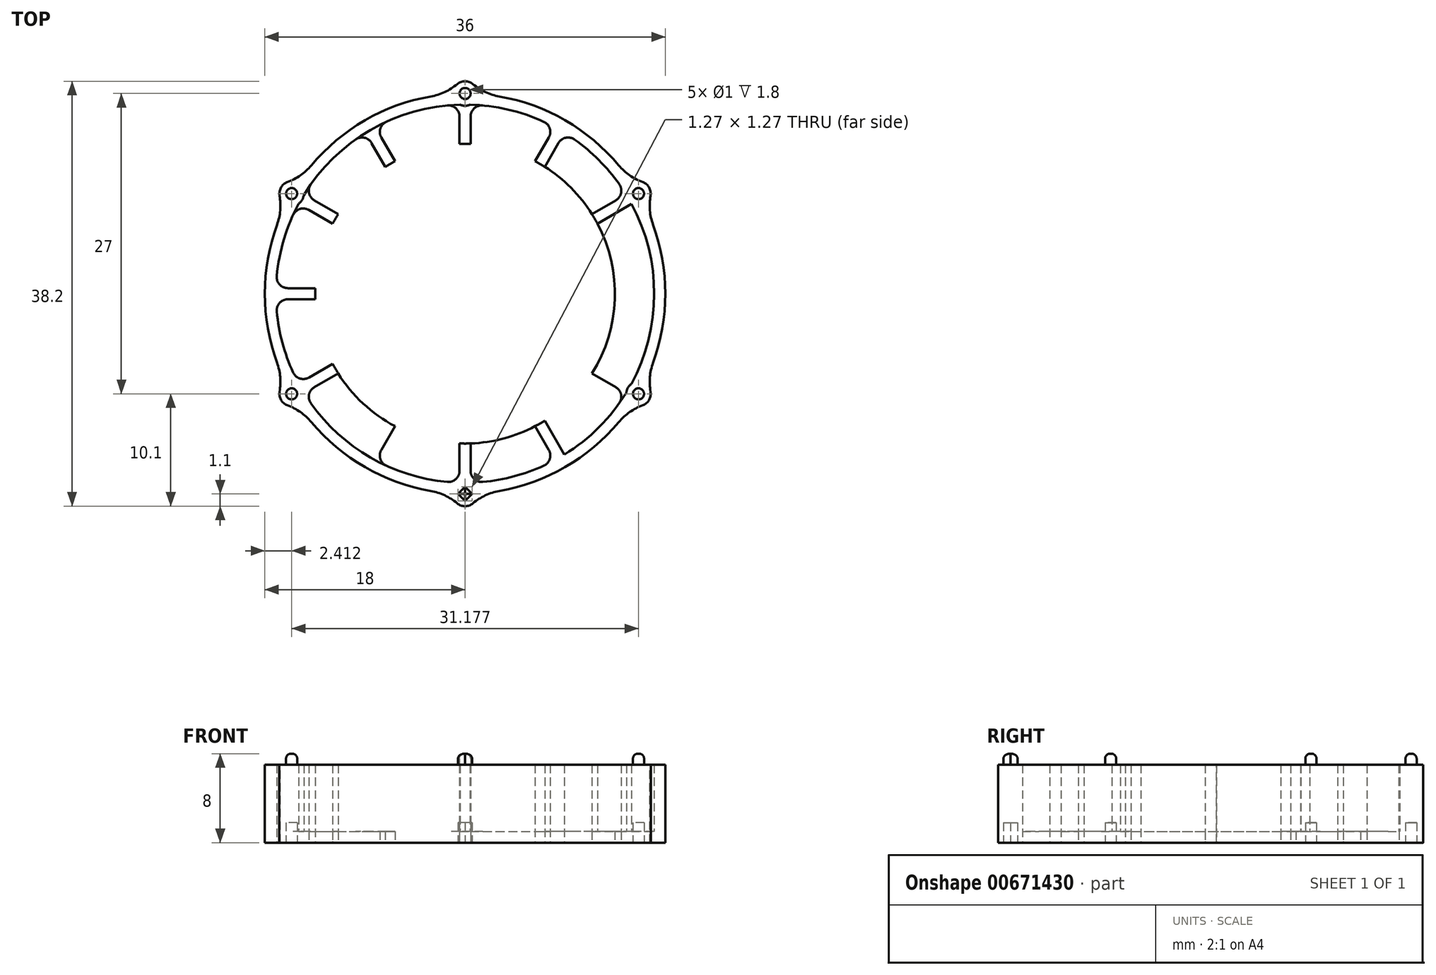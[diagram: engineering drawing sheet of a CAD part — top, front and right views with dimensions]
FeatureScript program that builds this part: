
annotation { "Feature Type Name" : "Feature", "Feature Type Description" : "" }
export const myFeature = defineFeature(function(context is Context, id is Id, definition is map)
    precondition{}
    {
        {
            var Q0;
            Q0=qCreatedBy(makeId("Top.planeOp"),FACE);
            var sketch = newSketch(context, id + "F0", { "sketchPlane" : qUnion([Q0])});
            skCircle(sketch, "E0", {"center": v(0, 0) * mm, "radius": 18 * mm});
            skCircle(sketch, "E1.0", {"center": v(0, 0) * mm, "radius": 17 * mm});
            skLineSegment(sketch, "E2.bottom", {"start": v(8.56, 15.83) * mm, "end": v(9.43, 15.33) * mm});
            skLineSegment(sketch, "E2.top", {"start": v(-9.43, -15.33) * mm, "end": v(-8.56, -15.83) * mm});
            skLineSegment(sketch, "E2.left", {"start": v(8.56, 15.83) * mm, "end": v(-9.43, -15.33) * mm});
            skLineSegment(sketch, "E2.right", {"start": v(9.43, 15.33) * mm, "end": v(-8.56, -15.83) * mm});
            skLineSegment(sketch, "E3.bottom", {"start": v(15.33, 9.43) * mm, "end": v(15.83, 8.56) * mm});
            skLineSegment(sketch, "E3.top", {"start": v(-15.83, -8.56) * mm, "end": v(-15.33, -9.43) * mm});
            skLineSegment(sketch, "E3.left", {"start": v(15.33, 9.43) * mm, "end": v(-15.83, -8.56) * mm});
            skLineSegment(sketch, "E3.right", {"start": v(15.83, 8.56) * mm, "end": v(-15.33, -9.43) * mm});
            skLineSegment(sketch, "E4", {"start": v(-38.35, 0) * mm, "end": v(39.17, 0) * mm, "construction": true});
            skLineSegment(sketch, "E5", {"start": v(0, 42.5) * mm, "end": v(0, -42.47) * mm, "construction": true});
            skLineSegment(sketch, "E6.bottom", {"start": v(-18, 0.5) * mm, "end": v(18, 0.5) * mm});
            skLineSegment(sketch, "E6.top", {"start": v(-18, -0.5) * mm, "end": v(18, -0.5) * mm});
            skLineSegment(sketch, "E6.left", {"start": v(-18, 0.5) * mm, "end": v(-18, -0.5) * mm});
            skLineSegment(sketch, "E6.right", {"start": v(18, 0.5) * mm, "end": v(18, -0.5) * mm});
            skLineSegment(sketch, "E7.bottom", {"start": v(-15.33, 9.43) * mm, "end": v(15.83, -8.56) * mm});
            skLineSegment(sketch, "E7.top", {"start": v(-15.83, 8.56) * mm, "end": v(15.33, -9.43) * mm});
            skLineSegment(sketch, "E7.left", {"start": v(-15.33, 9.43) * mm, "end": v(-15.83, 8.56) * mm});
            skLineSegment(sketch, "E7.right", {"start": v(15.83, -8.56) * mm, "end": v(15.33, -9.43) * mm});
            skLineSegment(sketch, "E8.bottom", {"start": v(-0.5, 18) * mm, "end": v(0.5, 18) * mm});
            skLineSegment(sketch, "E8.top", {"start": v(-0.5, -18) * mm, "end": v(0.5, -18) * mm});
            skLineSegment(sketch, "E8.left", {"start": v(-0.5, 18) * mm, "end": v(-0.5, -18) * mm});
            skLineSegment(sketch, "E8.right", {"start": v(0.5, 18) * mm, "end": v(0.5, -18) * mm});
            skLineSegment(sketch, "E9.bottom", {"start": v(-9.43, 15.33) * mm, "end": v(-8.56, 15.83) * mm});
            skLineSegment(sketch, "E9.top", {"start": v(8.56, -15.83) * mm, "end": v(9.43, -15.33) * mm});
            skLineSegment(sketch, "E9.left", {"start": v(-9.43, 15.33) * mm, "end": v(8.56, -15.83) * mm});
            skLineSegment(sketch, "E9.right", {"start": v(-8.56, 15.83) * mm, "end": v(9.43, -15.33) * mm});
            skCircle(sketch, "E10", {"center": v(0, 0) * mm, "radius": 13.47 * mm});
            skSolve(sketch);
        }
        {
            var Q0;
            Q0=qCreatedBy(makeId("Top.planeOp"),FACE);
            var sketch = newSketch(context, id + "F1", { "sketchPlane" : qUnion([Q0])});
            skCircle(sketch, "E11", {"center": v(0, 0) * mm, "radius": 18 * mm});
            skCircle(sketch, "E12", {"center": v(0, 0) * mm, "radius": 17 * mm});
            skSolve(sketch);
        }
        {
            var Q0;
            Q0=makeQuery(id+"F1.imprint","IMPRINT",FACE,{"disambiguationData":[TD([[makeQuery(id+"F1.imprint","IMPRINT",EDGE,{"derivedFrom":sQuery(id+"F1.wireOp",EDGE,"E11")}),1.0]])]});
            extrude(context, id + "F2", {"entities" : qUnion([Q0]), "depth" : 7 * mm, "offsetDistance" : 25 * mm});
        }
        {
            var Q0;
            {var subQ0=sQuery(id+"F0.wireOp",EDGE,"E2.right");var subQ1=sQuery(id+"F0.wireOp",EDGE,"E1.0");var subQ2=makeQuery(id+"F0.imprint","INTERSECT",VERTEX,{"disambiguationData":[OD(0.0)],"derivedFrom":[subQ1,subQ0]});Q0=makeQuery(id+"F0.imprint","IMPRINT",FACE,{"disambiguationData":[TD([[makeQuery(id+"F0.imprint","IMPRINT",EDGE,{"disambiguationData":[TD([[subQ2,-1.0]])],"derivedFrom":subQ1}),1.0]])]});}
            var Q1;
            {var subQ0=sQuery(id+"F0.wireOp",EDGE,"E8.left");var subQ1=sQuery(id+"F0.wireOp",EDGE,"E1.0");var subQ2=makeQuery(id+"F0.imprint","INTERSECT",VERTEX,{"disambiguationData":[OD(1.0)],"derivedFrom":[subQ1,subQ0]});Q1=makeQuery(id+"F0.imprint","IMPRINT",FACE,{"disambiguationData":[TD([[makeQuery(id+"F0.imprint","IMPRINT",EDGE,{"disambiguationData":[TD([[subQ2,-1.0]])],"derivedFrom":subQ1}),1.0]])]});}
            var Q2;
            {var subQ0=sQuery(id+"F0.wireOp",EDGE,"E3.left");var subQ1=sQuery(id+"F0.wireOp",EDGE,"E1.0");var subQ2=makeQuery(id+"F0.imprint","INTERSECT",VERTEX,{"disambiguationData":[OD(1.0)],"derivedFrom":[subQ1,subQ0]});Q2=makeQuery(id+"F0.imprint","IMPRINT",FACE,{"disambiguationData":[TD([[makeQuery(id+"F0.imprint","IMPRINT",EDGE,{"disambiguationData":[TD([[subQ2,-1.0]])],"derivedFrom":subQ1}),1.0]])]});}
            var Q3;
            {var subQ0=sQuery(id+"F0.wireOp",EDGE,"E3.right");var subQ1=sQuery(id+"F0.wireOp",EDGE,"E1.0");var subQ2=makeQuery(id+"F0.imprint","INTERSECT",VERTEX,{"disambiguationData":[OD(0.0)],"derivedFrom":[subQ1,subQ0]});Q3=makeQuery(id+"F0.imprint","IMPRINT",FACE,{"disambiguationData":[TD([[makeQuery(id+"F0.imprint","IMPRINT",EDGE,{"disambiguationData":[TD([[subQ2,-1.0]])],"derivedFrom":subQ1}),1.0]])]});}
            var Q4;
            {var subQ0=sQuery(id+"F0.wireOp",EDGE,"E9.left");var subQ1=sQuery(id+"F0.wireOp",EDGE,"E1.0");var subQ2=makeQuery(id+"F0.imprint","INTERSECT",VERTEX,{"disambiguationData":[OD(1.0)],"derivedFrom":[subQ1,subQ0]});Q4=makeQuery(id+"F0.imprint","IMPRINT",FACE,{"disambiguationData":[TD([[makeQuery(id+"F0.imprint","IMPRINT",EDGE,{"disambiguationData":[TD([[subQ2,-1.0]])],"derivedFrom":subQ1}),1.0]])]});}
            var Q5;
            {var subQ0=sQuery(id+"F0.wireOp",EDGE,"E6.bottom");var subQ1=sQuery(id+"F0.wireOp",EDGE,"E1.0");var subQ2=makeQuery(id+"F0.imprint","INTERSECT",VERTEX,{"disambiguationData":[OD(1.0)],"derivedFrom":[subQ1,subQ0]});Q5=makeQuery(id+"F0.imprint","IMPRINT",FACE,{"disambiguationData":[TD([[makeQuery(id+"F0.imprint","IMPRINT",EDGE,{"disambiguationData":[TD([[subQ2,-1.0]])],"derivedFrom":subQ1}),1.0]])]});}
            extrude(context, id + "F3", {"entities" : qUnion([Q0, Q1, Q2, Q3, Q4, Q5]), "operationType" : NewBodyOperationType.ADD, "depth" : 7 * mm, "offsetDistance" : 25 * mm});
        }
        {
            var Q0;
            Q0=makeQuery(id+"F1.imprint","IMPRINT",FACE,{"disambiguationData":[TD([[makeQuery(id+"F1.imprint","IMPRINT",EDGE,{"derivedFrom":sQuery(id+"F1.wireOp",EDGE,"E11")}),1.0]])]});
            var Q1;
            Q1=makeQuery(id+"F1.imprint","IMPRINT",FACE,{"disambiguationData":[TD([[makeQuery(id+"F1.imprint","IMPRINT",EDGE,{"derivedFrom":sQuery(id+"F1.wireOp",EDGE,"E12")}),1.0]])]});
            extrude(context, id + "F4", {"entities" : qUnion([Q0, Q1]), "operationType" : NewBodyOperationType.ADD, "depth" : 1 * mm, "offsetDistance" : 25 * mm});
        }
        {
            var Q0;
            Q0=qCreatedBy(makeId("Top.planeOp"),FACE);
            var sketch = newSketch(context, id + "F5", { "sketchPlane" : qUnion([Q0])});
            skCircle(sketch, "E13", {"center": v(0, 0) * mm, "radius": 18 * mm});
            skLineSegment(sketch, "E14", {"start": v(0, 18) * mm, "end": v(0, -18) * mm, "construction": true});
            skLineSegment(sketch, "E15", {"start": v(15.59, 9) * mm, "end": v(0, 0) * mm, "construction": true});
            skLineSegment(sketch, "E16", {"start": v(9, 15.59) * mm, "end": v(0, 0) * mm, "construction": true});
            skLineSegment(sketch, "E17", {"start": v(0, 0) * mm, "end": v(18, 0) * mm, "construction": true});
            skLineSegment(sketch, "E18", {"start": v(0, 0) * mm, "end": v(15.59, -9) * mm, "construction": true});
            skLineSegment(sketch, "E19", {"start": v(0, 0) * mm, "end": v(9, -15.59) * mm, "construction": true});
            skLineSegment(sketch, "E20", {"start": v(0, 0) * mm, "end": v(-9, 15.59) * mm, "construction": true});
            skLineSegment(sketch, "E21", {"start": v(0, 0) * mm, "end": v(-15.59, 9) * mm, "construction": true});
            skLineSegment(sketch, "E22", {"start": v(0, 0) * mm, "end": v(-18, 0) * mm, "construction": true});
            skLineSegment(sketch, "E23", {"start": v(0, 0) * mm, "end": v(-15.59, -9) * mm, "construction": true});
            skLineSegment(sketch, "E24", {"start": v(0, 0) * mm, "end": v(-9, -15.59) * mm, "construction": true});
            skCircle(sketch, "E25", {"center": v(0, 18) * mm, "radius": 1.1 * mm});
            skCircle(sketch, "E26", {"center": v(15.59, 9) * mm, "radius": 1.1 * mm});
            skCircle(sketch, "E27", {"center": v(15.59, -9) * mm, "radius": 1.1 * mm});
            skCircle(sketch, "E28", {"center": v(0, -18) * mm, "radius": 1.1 * mm});
            skCircle(sketch, "E29", {"center": v(-15.59, -9) * mm, "radius": 1.1 * mm});
            skCircle(sketch, "E30", {"center": v(-15.59, 9) * mm, "radius": 1.1 * mm});
            skCircle(sketch, "E31", {"center": v(-15.59, 9) * mm, "radius": 0.5 * mm});
            skCircle(sketch, "E32", {"center": v(0, 18) * mm, "radius": 0.5 * mm});
            skCircle(sketch, "E33", {"center": v(15.59, 9) * mm, "radius": 0.5 * mm});
            skCircle(sketch, "E34", {"center": v(15.59, -9) * mm, "radius": 0.5 * mm});
            skCircle(sketch, "E35", {"center": v(-15.59, -9) * mm, "radius": 0.5 * mm});
            skLineSegment(sketch, "E36.bottom", {"start": v(0.64, -18) * mm, "end": v(0, -18.64) * mm});
            skLineSegment(sketch, "E36.top", {"start": v(0, -17.36) * mm, "end": v(-0.64, -18) * mm});
            skLineSegment(sketch, "E36.left", {"start": v(0.64, -18) * mm, "end": v(0, -17.36) * mm});
            skLineSegment(sketch, "E36.right", {"start": v(0, -18.64) * mm, "end": v(-0.64, -18) * mm});
            skSolve(sketch);
        }
        {
            var Q0;
            {var subQ0=sQuery(id+"F5.wireOp",EDGE,"E30");var subQ1=sQuery(id+"F5.wireOp",EDGE,"E13");var subQ2=makeQuery(id+"F5.imprint","INTERSECT",VERTEX,{"disambiguationData":[OD(0.0)],"derivedFrom":[subQ1,subQ0]});Q0=makeQuery(id+"F5.imprint","IMPRINT",FACE,{"disambiguationData":[TD([[makeQuery(id+"F5.imprint","IMPRINT",EDGE,{"disambiguationData":[TD([[subQ2,-1.0]])],"derivedFrom":subQ1}),1.0]])]});}
            var Q1;
            {var subQ0=sQuery(id+"F5.wireOp",EDGE,"E30");var subQ1=sQuery(id+"F5.wireOp",EDGE,"E13");var subQ2=makeQuery(id+"F5.imprint","INTERSECT",VERTEX,{"disambiguationData":[OD(0.0)],"derivedFrom":[subQ1,subQ0]});Q1=makeQuery(id+"F5.imprint","IMPRINT",FACE,{"disambiguationData":[TD([[makeQuery(id+"F5.imprint","IMPRINT",EDGE,{"disambiguationData":[TD([[subQ2,-1.0]])],"derivedFrom":subQ1}),-1.0]])]});}
            var Q2;
            {var subQ0=sQuery(id+"F5.wireOp",EDGE,"E25");var subQ1=sQuery(id+"F5.wireOp",EDGE,"E13");var subQ2=makeQuery(id+"F5.imprint","INTERSECT",VERTEX,{"disambiguationData":[OD(0.0)],"derivedFrom":[subQ1,subQ0]});Q2=makeQuery(id+"F5.imprint","IMPRINT",FACE,{"disambiguationData":[TD([[makeQuery(id+"F5.imprint","IMPRINT",EDGE,{"disambiguationData":[TD([[subQ2,-1.0]])],"derivedFrom":subQ1}),1.0]])]});}
            var Q3;
            {var subQ0=sQuery(id+"F5.wireOp",EDGE,"E25");var subQ1=sQuery(id+"F5.wireOp",EDGE,"E13");var subQ2=makeQuery(id+"F5.imprint","INTERSECT",VERTEX,{"disambiguationData":[OD(0.0)],"derivedFrom":[subQ1,subQ0]});Q3=makeQuery(id+"F5.imprint","IMPRINT",FACE,{"disambiguationData":[TD([[makeQuery(id+"F5.imprint","IMPRINT",EDGE,{"disambiguationData":[TD([[subQ2,-1.0]])],"derivedFrom":subQ1}),-1.0]])]});}
            var Q4;
            {var subQ0=sQuery(id+"F5.wireOp",EDGE,"E26");var subQ1=sQuery(id+"F5.wireOp",EDGE,"E13");var subQ2=makeQuery(id+"F5.imprint","INTERSECT",VERTEX,{"disambiguationData":[OD(0.0)],"derivedFrom":[subQ1,subQ0]});Q4=makeQuery(id+"F5.imprint","IMPRINT",FACE,{"disambiguationData":[TD([[makeQuery(id+"F5.imprint","IMPRINT",EDGE,{"disambiguationData":[TD([[subQ2,-1.0]])],"derivedFrom":subQ1}),-1.0]])]});}
            var Q5;
            {var subQ0=sQuery(id+"F5.wireOp",EDGE,"E26");var subQ1=sQuery(id+"F5.wireOp",EDGE,"E13");var subQ2=makeQuery(id+"F5.imprint","INTERSECT",VERTEX,{"disambiguationData":[OD(0.0)],"derivedFrom":[subQ1,subQ0]});Q5=makeQuery(id+"F5.imprint","IMPRINT",FACE,{"disambiguationData":[TD([[makeQuery(id+"F5.imprint","IMPRINT",EDGE,{"disambiguationData":[TD([[subQ2,-1.0]])],"derivedFrom":subQ1}),1.0]])]});}
            var Q6;
            {var subQ0=sQuery(id+"F5.wireOp",EDGE,"E29");var subQ1=sQuery(id+"F5.wireOp",EDGE,"E13");var subQ2=makeQuery(id+"F5.imprint","INTERSECT",VERTEX,{"disambiguationData":[OD(0.0)],"derivedFrom":[subQ1,subQ0]});Q6=makeQuery(id+"F5.imprint","IMPRINT",FACE,{"disambiguationData":[TD([[makeQuery(id+"F5.imprint","IMPRINT",EDGE,{"disambiguationData":[TD([[subQ2,-1.0]])],"derivedFrom":subQ1}),1.0]])]});}
            var Q7;
            {var subQ0=sQuery(id+"F5.wireOp",EDGE,"E29");var subQ1=sQuery(id+"F5.wireOp",EDGE,"E13");var subQ2=makeQuery(id+"F5.imprint","INTERSECT",VERTEX,{"disambiguationData":[OD(0.0)],"derivedFrom":[subQ1,subQ0]});Q7=makeQuery(id+"F5.imprint","IMPRINT",FACE,{"disambiguationData":[TD([[makeQuery(id+"F5.imprint","IMPRINT",EDGE,{"disambiguationData":[TD([[subQ2,-1.0]])],"derivedFrom":subQ1}),-1.0]])]});}
            var Q8;
            {var subQ3=sQuery(id+"F5.wireOp",EDGE,"E13");var subQ5=sQuery(id+"F5.wireOp",EDGE,"E28");var subQ6=makeQuery(id+"F5.imprint","INTERSECT",VERTEX,{"disambiguationData":[OD(0.0)],"derivedFrom":[subQ3,subQ5]});Q8=makeQuery(id+"F5.imprint","IMPRINT",FACE,{"disambiguationData":[TD([[makeQuery(id+"F5.imprint","IMPRINT",EDGE,{"disambiguationData":[TD([[subQ6,-1.0]])],"derivedFrom":subQ3}),1.0]])]});}
            var Q9;
            {var subQ6=sQuery(id+"F5.wireOp",EDGE,"E36.bottom");Q9=makeQuery(id+"F5.imprint","IMPRINT",FACE,{"disambiguationData":[TD([[makeQuery(id+"F5.imprint","IMPRINT",EDGE,{"derivedFrom":subQ6}),1.0]])]});}
            var Q10;
            {var subQ0=sQuery(id+"F5.wireOp",EDGE,"E27");var subQ1=sQuery(id+"F5.wireOp",EDGE,"E13");var subQ2=makeQuery(id+"F5.imprint","INTERSECT",VERTEX,{"disambiguationData":[OD(0.0)],"derivedFrom":[subQ1,subQ0]});Q10=makeQuery(id+"F5.imprint","IMPRINT",FACE,{"disambiguationData":[TD([[makeQuery(id+"F5.imprint","IMPRINT",EDGE,{"disambiguationData":[TD([[subQ2,-1.0]])],"derivedFrom":subQ1}),-1.0]])]});}
            var Q11;
            {var subQ0=sQuery(id+"F5.wireOp",EDGE,"E27");var subQ1=sQuery(id+"F5.wireOp",EDGE,"E13");var subQ2=makeQuery(id+"F5.imprint","INTERSECT",VERTEX,{"disambiguationData":[OD(0.0)],"derivedFrom":[subQ1,subQ0]});Q11=makeQuery(id+"F5.imprint","IMPRINT",FACE,{"disambiguationData":[TD([[makeQuery(id+"F5.imprint","IMPRINT",EDGE,{"disambiguationData":[TD([[subQ2,-1.0]])],"derivedFrom":subQ1}),1.0]])]});}
            var Q12;
            {var subQ0=sQuery(id+"F5.wireOp",EDGE,"E31");var subQ1=sQuery(id+"F5.wireOp",EDGE,"E13");var subQ2=makeQuery(id+"F5.imprint","INTERSECT",VERTEX,{"disambiguationData":[OD(0.0)],"derivedFrom":[subQ1,subQ0]});Q12=makeQuery(id+"F5.imprint","IMPRINT",FACE,{"disambiguationData":[TD([[makeQuery(id+"F5.imprint","IMPRINT",EDGE,{"disambiguationData":[TD([[subQ2,-1.0]])],"derivedFrom":subQ1}),1.0]])]});}
            var Q13;
            {var subQ0=sQuery(id+"F5.wireOp",EDGE,"E31");var subQ1=sQuery(id+"F5.wireOp",EDGE,"E13");var subQ2=makeQuery(id+"F5.imprint","INTERSECT",VERTEX,{"disambiguationData":[OD(0.0)],"derivedFrom":[subQ1,subQ0]});Q13=makeQuery(id+"F5.imprint","IMPRINT",FACE,{"disambiguationData":[TD([[makeQuery(id+"F5.imprint","IMPRINT",EDGE,{"disambiguationData":[TD([[subQ2,-1.0]])],"derivedFrom":subQ1}),-1.0]])]});}
            var Q14;
            {var subQ0=sQuery(id+"F5.wireOp",EDGE,"E32");var subQ1=sQuery(id+"F5.wireOp",EDGE,"E13");var subQ2=makeQuery(id+"F5.imprint","INTERSECT",VERTEX,{"disambiguationData":[OD(0.0)],"derivedFrom":[subQ1,subQ0]});Q14=makeQuery(id+"F5.imprint","IMPRINT",FACE,{"disambiguationData":[TD([[makeQuery(id+"F5.imprint","IMPRINT",EDGE,{"disambiguationData":[TD([[subQ2,-1.0]])],"derivedFrom":subQ1}),-1.0]])]});}
            var Q15;
            {var subQ0=sQuery(id+"F5.wireOp",EDGE,"E32");var subQ1=sQuery(id+"F5.wireOp",EDGE,"E13");var subQ2=makeQuery(id+"F5.imprint","INTERSECT",VERTEX,{"disambiguationData":[OD(0.0)],"derivedFrom":[subQ1,subQ0]});Q15=makeQuery(id+"F5.imprint","IMPRINT",FACE,{"disambiguationData":[TD([[makeQuery(id+"F5.imprint","IMPRINT",EDGE,{"disambiguationData":[TD([[subQ2,-1.0]])],"derivedFrom":subQ1}),1.0]])]});}
            var Q16;
            {var subQ0=sQuery(id+"F5.wireOp",EDGE,"E33");var subQ1=sQuery(id+"F5.wireOp",EDGE,"E13");var subQ2=makeQuery(id+"F5.imprint","INTERSECT",VERTEX,{"disambiguationData":[OD(0.0)],"derivedFrom":[subQ1,subQ0]});Q16=makeQuery(id+"F5.imprint","IMPRINT",FACE,{"disambiguationData":[TD([[makeQuery(id+"F5.imprint","IMPRINT",EDGE,{"disambiguationData":[TD([[subQ2,-1.0]])],"derivedFrom":subQ1}),-1.0]])]});}
            var Q17;
            {var subQ0=sQuery(id+"F5.wireOp",EDGE,"E33");var subQ1=sQuery(id+"F5.wireOp",EDGE,"E13");var subQ2=makeQuery(id+"F5.imprint","INTERSECT",VERTEX,{"disambiguationData":[OD(0.0)],"derivedFrom":[subQ1,subQ0]});Q17=makeQuery(id+"F5.imprint","IMPRINT",FACE,{"disambiguationData":[TD([[makeQuery(id+"F5.imprint","IMPRINT",EDGE,{"disambiguationData":[TD([[subQ2,-1.0]])],"derivedFrom":subQ1}),1.0]])]});}
            var Q18;
            {var subQ0=sQuery(id+"F5.wireOp",EDGE,"E34");var subQ1=sQuery(id+"F5.wireOp",EDGE,"E13");var subQ2=makeQuery(id+"F5.imprint","INTERSECT",VERTEX,{"disambiguationData":[OD(0.0)],"derivedFrom":[subQ1,subQ0]});Q18=makeQuery(id+"F5.imprint","IMPRINT",FACE,{"disambiguationData":[TD([[makeQuery(id+"F5.imprint","IMPRINT",EDGE,{"disambiguationData":[TD([[subQ2,-1.0]])],"derivedFrom":subQ1}),-1.0]])]});}
            var Q19;
            {var subQ0=sQuery(id+"F5.wireOp",EDGE,"E34");var subQ1=sQuery(id+"F5.wireOp",EDGE,"E13");var subQ2=makeQuery(id+"F5.imprint","INTERSECT",VERTEX,{"disambiguationData":[OD(0.0)],"derivedFrom":[subQ1,subQ0]});Q19=makeQuery(id+"F5.imprint","IMPRINT",FACE,{"disambiguationData":[TD([[makeQuery(id+"F5.imprint","IMPRINT",EDGE,{"disambiguationData":[TD([[subQ2,-1.0]])],"derivedFrom":subQ1}),1.0]])]});}
            var Q20;
            {var subQ1=sQuery(id+"F5.wireOp",EDGE,"E36.bottom");Q20=makeQuery(id+"F5.imprint","IMPRINT",FACE,{"disambiguationData":[TD([[makeQuery(id+"F5.imprint","IMPRINT",EDGE,{"derivedFrom":subQ1}),-1.0]])]});}
            var Q21;
            {var subQ0=sQuery(id+"F5.wireOp",EDGE,"E35");var subQ1=sQuery(id+"F5.wireOp",EDGE,"E13");var subQ2=makeQuery(id+"F5.imprint","INTERSECT",VERTEX,{"disambiguationData":[OD(0.0)],"derivedFrom":[subQ1,subQ0]});Q21=makeQuery(id+"F5.imprint","IMPRINT",FACE,{"disambiguationData":[TD([[makeQuery(id+"F5.imprint","IMPRINT",EDGE,{"disambiguationData":[TD([[subQ2,-1.0]])],"derivedFrom":subQ1}),-1.0]])]});}
            var Q22;
            {var subQ0=sQuery(id+"F5.wireOp",EDGE,"E35");var subQ1=sQuery(id+"F5.wireOp",EDGE,"E13");var subQ2=makeQuery(id+"F5.imprint","INTERSECT",VERTEX,{"disambiguationData":[OD(0.0)],"derivedFrom":[subQ1,subQ0]});Q22=makeQuery(id+"F5.imprint","IMPRINT",FACE,{"disambiguationData":[TD([[makeQuery(id+"F5.imprint","IMPRINT",EDGE,{"disambiguationData":[TD([[subQ2,-1.0]])],"derivedFrom":subQ1}),1.0]])]});}
            var Q23;
            {var subQ0=sQuery(id+"F5.wireOp",EDGE,"E36.top");var subQ1=sQuery(id+"F5.wireOp",EDGE,"E13");var subQ2=makeQuery(id+"F5.imprint","INTERSECT",VERTEX,{"derivedFrom":[subQ1,subQ0]});Q23=makeQuery(id+"F5.imprint","IMPRINT",FACE,{"disambiguationData":[TD([[makeQuery(id+"F5.imprint","IMPRINT",EDGE,{"disambiguationData":[TD([[subQ2,-1.0]])],"derivedFrom":subQ1}),1.0]])]});}
            extrude(context, id + "F6", {"entities" : qUnion([Q0, Q1, Q2, Q3, Q4, Q5, Q6, Q7, Q8, Q9, Q10, Q11, Q12, Q13, Q14, Q15, Q16, Q17, Q18, Q19, Q20, Q21, Q22, Q23]), "operationType" : NewBodyOperationType.ADD, "depth" : 7 * mm, "offsetDistance" : 25 * mm});
        }
        {
            var Q0;
            {var subQ0=sQuery(id+"F0.wireOp",EDGE,"E8.right");var subQ1=sQuery(id+"F0.wireOp",EDGE,"E1.0");Q0=makeQuery(id+"F3.opExtrude","SWEPT_EDGE",EDGE,{"disambiguationData":[OSD([subQ1,subQ0]),TDD([makeQuery(id+"F0.imprint","INTERSECT",VERTEX,{"disambiguationData":[OD(1.0)],"derivedFrom":[subQ1,subQ0]})])]});}
            var Q1;
            {var subQ0=sQuery(id+"F0.wireOp",EDGE,"E2.left");var subQ1=sQuery(id+"F0.wireOp",EDGE,"E1.0");Q1=makeQuery(id+"F3.opExtrude","SWEPT_EDGE",EDGE,{"disambiguationData":[OSD([subQ1,subQ0]),TDD([makeQuery(id+"F0.imprint","INTERSECT",VERTEX,{"disambiguationData":[OD(1.0)],"derivedFrom":[subQ1,subQ0]})])]});}
            var Q2;
            {var subQ0=sQuery(id+"F0.wireOp",EDGE,"E3.left");var subQ1=sQuery(id+"F0.wireOp",EDGE,"E1.0");Q2=makeQuery(id+"F3.opExtrude","SWEPT_EDGE",EDGE,{"disambiguationData":[OSD([subQ1,subQ0]),TDD([makeQuery(id+"F0.imprint","INTERSECT",VERTEX,{"disambiguationData":[OD(1.0)],"derivedFrom":[subQ1,subQ0]})])]});}
            var Q3;
            {var subQ0=sQuery(id+"F0.wireOp",EDGE,"E6.bottom");var subQ1=sQuery(id+"F0.wireOp",EDGE,"E1.0");Q3=makeQuery(id+"F3.opExtrude","SWEPT_EDGE",EDGE,{"disambiguationData":[OSD([subQ1,subQ0]),TDD([makeQuery(id+"F0.imprint","INTERSECT",VERTEX,{"disambiguationData":[OD(1.0)],"derivedFrom":[subQ1,subQ0]})])]});}
            var Q4;
            {var subQ0=sQuery(id+"F0.wireOp",EDGE,"E9.right");var subQ1=sQuery(id+"F0.wireOp",EDGE,"E1.0");Q4=makeQuery(id+"F3.opExtrude","SWEPT_EDGE",EDGE,{"disambiguationData":[OSD([subQ1,subQ0]),TDD([makeQuery(id+"F0.imprint","INTERSECT",VERTEX,{"disambiguationData":[OD(1.0)],"derivedFrom":[subQ1,subQ0]})])]});}
            var Q5;
            {var subQ0=sQuery(id+"F0.wireOp",EDGE,"E7.bottom");var subQ1=sQuery(id+"F0.wireOp",EDGE,"E1.0");Q5=makeQuery(id+"F3.opExtrude","SWEPT_EDGE",EDGE,{"disambiguationData":[OSD([subQ1,subQ0]),TDD([makeQuery(id+"F0.imprint","INTERSECT",VERTEX,{"disambiguationData":[OD(1.0)],"derivedFrom":[subQ1,subQ0]})])]});}
            var Q6;
            {var subQ0=sQuery(id+"F0.wireOp",EDGE,"E8.left");var subQ1=sQuery(id+"F0.wireOp",EDGE,"E1.0");Q6=makeQuery(id+"F3.opExtrude","SWEPT_EDGE",EDGE,{"disambiguationData":[OSD([subQ1,subQ0]),TDD([makeQuery(id+"F0.imprint","INTERSECT",VERTEX,{"disambiguationData":[OD(0.0)],"derivedFrom":[subQ1,subQ0]})])]});}
            var Q7;
            {var subQ0=sQuery(id+"F0.wireOp",EDGE,"E2.left");var subQ1=sQuery(id+"F0.wireOp",EDGE,"E1.0");Q7=makeQuery(id+"F3.opExtrude","SWEPT_EDGE",EDGE,{"disambiguationData":[OSD([subQ1,subQ0]),TDD([makeQuery(id+"F0.imprint","INTERSECT",VERTEX,{"disambiguationData":[OD(0.0)],"derivedFrom":[subQ1,subQ0]})])]});}
            var Q8;
            {var subQ0=sQuery(id+"F0.wireOp",EDGE,"E3.left");var subQ1=sQuery(id+"F0.wireOp",EDGE,"E1.0");Q8=makeQuery(id+"F3.opExtrude","SWEPT_EDGE",EDGE,{"disambiguationData":[OSD([subQ1,subQ0]),TDD([makeQuery(id+"F0.imprint","INTERSECT",VERTEX,{"disambiguationData":[OD(0.0)],"derivedFrom":[subQ1,subQ0]})])]});}
            var Q9;
            {var subQ0=sQuery(id+"F0.wireOp",EDGE,"E6.top");var subQ1=sQuery(id+"F0.wireOp",EDGE,"E1.0");Q9=makeQuery(id+"F3.opExtrude","SWEPT_EDGE",EDGE,{"disambiguationData":[OSD([subQ1,subQ0]),TDD([makeQuery(id+"F0.imprint","INTERSECT",VERTEX,{"disambiguationData":[OD(1.0)],"derivedFrom":[subQ1,subQ0]})])]});}
            var Q10;
            {var subQ0=sQuery(id+"F0.wireOp",EDGE,"E7.top");var subQ1=sQuery(id+"F0.wireOp",EDGE,"E1.0");Q10=makeQuery(id+"F3.opExtrude","SWEPT_EDGE",EDGE,{"disambiguationData":[OSD([subQ1,subQ0]),TDD([makeQuery(id+"F0.imprint","INTERSECT",VERTEX,{"disambiguationData":[OD(0.0)],"derivedFrom":[subQ1,subQ0]})])]});}
            var Q11;
            {var subQ0=sQuery(id+"F0.wireOp",EDGE,"E6.top");var subQ1=sQuery(id+"F0.wireOp",EDGE,"E1.0");Q11=makeQuery(id+"F3.opExtrude","SWEPT_EDGE",EDGE,{"disambiguationData":[OSD([subQ1,subQ0]),TDD([makeQuery(id+"F0.imprint","INTERSECT",VERTEX,{"disambiguationData":[OD(0.0)],"derivedFrom":[subQ1,subQ0]})])]});}
            var Q12;
            {var subQ0=sQuery(id+"F0.wireOp",EDGE,"E9.left");var subQ1=sQuery(id+"F0.wireOp",EDGE,"E1.0");Q12=makeQuery(id+"F3.opExtrude","SWEPT_EDGE",EDGE,{"disambiguationData":[OSD([subQ1,subQ0]),TDD([makeQuery(id+"F0.imprint","INTERSECT",VERTEX,{"disambiguationData":[OD(0.0)],"derivedFrom":[subQ1,subQ0]})])]});}
            var Q13;
            {var subQ0=sQuery(id+"F0.wireOp",EDGE,"E8.right");var subQ1=sQuery(id+"F0.wireOp",EDGE,"E1.0");Q13=makeQuery(id+"F3.opExtrude","SWEPT_EDGE",EDGE,{"disambiguationData":[OSD([subQ1,subQ0]),TDD([makeQuery(id+"F0.imprint","INTERSECT",VERTEX,{"disambiguationData":[OD(0.0)],"derivedFrom":[subQ1,subQ0]})])]});}
            var Q14;
            {var subQ0=sQuery(id+"F0.wireOp",EDGE,"E7.bottom");var subQ1=sQuery(id+"F0.wireOp",EDGE,"E1.0");Q14=makeQuery(id+"F3.opExtrude","SWEPT_EDGE",EDGE,{"disambiguationData":[OSD([subQ1,subQ0]),TDD([makeQuery(id+"F0.imprint","INTERSECT",VERTEX,{"disambiguationData":[OD(0.0)],"derivedFrom":[subQ1,subQ0]})])]});}
            var Q15;
            {var subQ0=sQuery(id+"F0.wireOp",EDGE,"E9.right");var subQ1=sQuery(id+"F0.wireOp",EDGE,"E1.0");Q15=makeQuery(id+"F3.opExtrude","SWEPT_EDGE",EDGE,{"disambiguationData":[OSD([subQ1,subQ0]),TDD([makeQuery(id+"F0.imprint","INTERSECT",VERTEX,{"disambiguationData":[OD(0.0)],"derivedFrom":[subQ1,subQ0]})])]});}
            var Q16;
            {var subQ0=sQuery(id+"F0.wireOp",EDGE,"E3.right");var subQ1=sQuery(id+"F0.wireOp",EDGE,"E1.0");Q16=makeQuery(id+"F3.opExtrude","SWEPT_EDGE",EDGE,{"disambiguationData":[OSD([subQ1,subQ0]),TDD([makeQuery(id+"F0.imprint","INTERSECT",VERTEX,{"disambiguationData":[OD(1.0)],"derivedFrom":[subQ1,subQ0]})])]});}
            var Q17;
            {var subQ0=sQuery(id+"F0.wireOp",EDGE,"E2.right");var subQ1=sQuery(id+"F0.wireOp",EDGE,"E1.0");Q17=makeQuery(id+"F3.opExtrude","SWEPT_EDGE",EDGE,{"disambiguationData":[OSD([subQ1,subQ0]),TDD([makeQuery(id+"F0.imprint","INTERSECT",VERTEX,{"disambiguationData":[OD(1.0)],"derivedFrom":[subQ1,subQ0]})])]});}
            var Q18;
            {var subQ0=sQuery(id+"F0.wireOp",EDGE,"E3.right");var subQ1=sQuery(id+"F0.wireOp",EDGE,"E1.0");Q18=makeQuery(id+"F3.opExtrude","SWEPT_EDGE",EDGE,{"disambiguationData":[OSD([subQ1,subQ0]),TDD([makeQuery(id+"F0.imprint","INTERSECT",VERTEX,{"disambiguationData":[OD(0.0)],"derivedFrom":[subQ1,subQ0]})])]});}
            var Q19;
            {var subQ0=sQuery(id+"F0.wireOp",EDGE,"E2.right");var subQ1=sQuery(id+"F0.wireOp",EDGE,"E1.0");Q19=makeQuery(id+"F3.opExtrude","SWEPT_EDGE",EDGE,{"disambiguationData":[OSD([subQ1,subQ0]),TDD([makeQuery(id+"F0.imprint","INTERSECT",VERTEX,{"disambiguationData":[OD(0.0)],"derivedFrom":[subQ1,subQ0]})])]});}
            var Q20;
            {var subQ0=sQuery(id+"F0.wireOp",EDGE,"E8.left");var subQ1=sQuery(id+"F0.wireOp",EDGE,"E1.0");Q20=makeQuery(id+"F3.opExtrude","SWEPT_EDGE",EDGE,{"disambiguationData":[OSD([subQ1,subQ0]),TDD([makeQuery(id+"F0.imprint","INTERSECT",VERTEX,{"disambiguationData":[OD(1.0)],"derivedFrom":[subQ1,subQ0]})])]});}
            var Q21;
            {var subQ0=sQuery(id+"F0.wireOp",EDGE,"E9.left");var subQ1=sQuery(id+"F0.wireOp",EDGE,"E1.0");Q21=makeQuery(id+"F3.opExtrude","SWEPT_EDGE",EDGE,{"disambiguationData":[OSD([subQ1,subQ0]),TDD([makeQuery(id+"F0.imprint","INTERSECT",VERTEX,{"disambiguationData":[OD(1.0)],"derivedFrom":[subQ1,subQ0]})])]});}
            var Q22;
            {var subQ0=sQuery(id+"F0.wireOp",EDGE,"E7.top");var subQ1=sQuery(id+"F0.wireOp",EDGE,"E1.0");Q22=makeQuery(id+"F3.opExtrude","SWEPT_EDGE",EDGE,{"disambiguationData":[OSD([subQ1,subQ0]),TDD([makeQuery(id+"F0.imprint","INTERSECT",VERTEX,{"disambiguationData":[OD(1.0)],"derivedFrom":[subQ1,subQ0]})])]});}
            var Q23;
            {var subQ0=sQuery(id+"F0.wireOp",EDGE,"E6.bottom");var subQ1=sQuery(id+"F0.wireOp",EDGE,"E1.0");Q23=makeQuery(id+"F3.opExtrude","SWEPT_EDGE",EDGE,{"disambiguationData":[OSD([subQ1,subQ0]),TDD([makeQuery(id+"F0.imprint","INTERSECT",VERTEX,{"disambiguationData":[OD(0.0)],"derivedFrom":[subQ1,subQ0]})])]});}
            fillet(context, id + "F7", {"entities" : qUnion([Q0, Q1, Q2, Q3, Q4, Q5, Q6, Q7, Q8, Q9, Q10, Q11, Q12, Q13, Q14, Q15, Q16, Q17, Q18, Q19, Q20, Q21, Q22, Q23]), "radius" : 1 * mm, "tangentPropagation" : true, "allowEdgeOverflow" : false});
        }
        {
            var Q0;
            Q0=makeQuery(id+"F6.boolean.opBoolean","INTERSECT",EDGE,{"disambiguationData":[OD(0.0)],"derivedFrom":[makeQuery(id+"F2.opExtrude","SWEPT_FACE",FACE,{"disambiguationData":[OSD([sQuery(id+"F1.wireOp",EDGE,"E11")])]}),makeQuery(id+"F6.opExtrude","SWEPT_FACE",FACE,{"disambiguationData":[OSD([sQuery(id+"F5.wireOp",EDGE,"E30")])]})]});
            var Q1;
            Q1=makeQuery(id+"F6.boolean.opBoolean","INTERSECT",EDGE,{"disambiguationData":[OD(1.0)],"derivedFrom":[makeQuery(id+"F2.opExtrude","SWEPT_FACE",FACE,{"disambiguationData":[OSD([sQuery(id+"F1.wireOp",EDGE,"E11")])]}),makeQuery(id+"F6.opExtrude","SWEPT_FACE",FACE,{"disambiguationData":[OSD([sQuery(id+"F5.wireOp",EDGE,"E30")])]})]});
            var Q2;
            Q2=makeQuery(id+"F6.boolean.opBoolean","INTERSECT",EDGE,{"disambiguationData":[OD(1.0)],"derivedFrom":[makeQuery(id+"F2.opExtrude","SWEPT_FACE",FACE,{"disambiguationData":[OSD([sQuery(id+"F1.wireOp",EDGE,"E11")])]}),makeQuery(id+"F6.opExtrude","SWEPT_FACE",FACE,{"disambiguationData":[OSD([sQuery(id+"F5.wireOp",EDGE,"E25")])]})]});
            var Q3;
            Q3=makeQuery(id+"F6.boolean.opBoolean","INTERSECT",EDGE,{"disambiguationData":[OD(1.0)],"derivedFrom":[makeQuery(id+"F2.opExtrude","SWEPT_FACE",FACE,{"disambiguationData":[OSD([sQuery(id+"F1.wireOp",EDGE,"E11")])]}),makeQuery(id+"F6.opExtrude","SWEPT_FACE",FACE,{"disambiguationData":[OSD([sQuery(id+"F5.wireOp",EDGE,"E29")])]})]});
            var Q4;
            Q4=makeQuery(id+"F6.boolean.opBoolean","INTERSECT",EDGE,{"disambiguationData":[OD(0.0)],"derivedFrom":[makeQuery(id+"F2.opExtrude","SWEPT_FACE",FACE,{"disambiguationData":[OSD([sQuery(id+"F1.wireOp",EDGE,"E11")])]}),makeQuery(id+"F6.opExtrude","SWEPT_FACE",FACE,{"disambiguationData":[OSD([sQuery(id+"F5.wireOp",EDGE,"E29")])]})]});
            var Q5;
            Q5=makeQuery(id+"F6.boolean.opBoolean","INTERSECT",EDGE,{"disambiguationData":[OD(1.0)],"derivedFrom":[makeQuery(id+"F2.opExtrude","SWEPT_FACE",FACE,{"disambiguationData":[OSD([sQuery(id+"F1.wireOp",EDGE,"E11")])]}),makeQuery(id+"F6.opExtrude","SWEPT_FACE",FACE,{"disambiguationData":[OSD([sQuery(id+"F5.wireOp",EDGE,"E28")])]})]});
            var Q6;
            Q6=makeQuery(id+"F6.boolean.opBoolean","INTERSECT",EDGE,{"disambiguationData":[OD(0.0)],"derivedFrom":[makeQuery(id+"F2.opExtrude","SWEPT_FACE",FACE,{"disambiguationData":[OSD([sQuery(id+"F1.wireOp",EDGE,"E11")])]}),makeQuery(id+"F6.opExtrude","SWEPT_FACE",FACE,{"disambiguationData":[OSD([sQuery(id+"F5.wireOp",EDGE,"E28")])]})]});
            var Q7;
            Q7=makeQuery(id+"F6.boolean.opBoolean","INTERSECT",EDGE,{"disambiguationData":[OD(1.0)],"derivedFrom":[makeQuery(id+"F2.opExtrude","SWEPT_FACE",FACE,{"disambiguationData":[OSD([sQuery(id+"F1.wireOp",EDGE,"E11")])]}),makeQuery(id+"F6.opExtrude","SWEPT_FACE",FACE,{"disambiguationData":[OSD([sQuery(id+"F5.wireOp",EDGE,"E27")])]})]});
            var Q8;
            Q8=makeQuery(id+"F6.boolean.opBoolean","INTERSECT",EDGE,{"disambiguationData":[OD(0.0)],"derivedFrom":[makeQuery(id+"F2.opExtrude","SWEPT_FACE",FACE,{"disambiguationData":[OSD([sQuery(id+"F1.wireOp",EDGE,"E11")])]}),makeQuery(id+"F6.opExtrude","SWEPT_FACE",FACE,{"disambiguationData":[OSD([sQuery(id+"F5.wireOp",EDGE,"E27")])]})]});
            var Q9;
            Q9=makeQuery(id+"F6.boolean.opBoolean","INTERSECT",EDGE,{"disambiguationData":[OD(1.0)],"derivedFrom":[makeQuery(id+"F2.opExtrude","SWEPT_FACE",FACE,{"disambiguationData":[OSD([sQuery(id+"F1.wireOp",EDGE,"E11")])]}),makeQuery(id+"F6.opExtrude","SWEPT_FACE",FACE,{"disambiguationData":[OSD([sQuery(id+"F5.wireOp",EDGE,"E26")])]})]});
            var Q10;
            Q10=makeQuery(id+"F6.boolean.opBoolean","INTERSECT",EDGE,{"disambiguationData":[OD(0.0)],"derivedFrom":[makeQuery(id+"F2.opExtrude","SWEPT_FACE",FACE,{"disambiguationData":[OSD([sQuery(id+"F1.wireOp",EDGE,"E11")])]}),makeQuery(id+"F6.opExtrude","SWEPT_FACE",FACE,{"disambiguationData":[OSD([sQuery(id+"F5.wireOp",EDGE,"E26")])]})]});
            var Q11;
            Q11=makeQuery(id+"F6.boolean.opBoolean","INTERSECT",EDGE,{"disambiguationData":[OD(0.0)],"derivedFrom":[makeQuery(id+"F2.opExtrude","SWEPT_FACE",FACE,{"disambiguationData":[OSD([sQuery(id+"F1.wireOp",EDGE,"E11")])]}),makeQuery(id+"F6.opExtrude","SWEPT_FACE",FACE,{"disambiguationData":[OSD([sQuery(id+"F5.wireOp",EDGE,"E25")])]})]});
            fillet(context, id + "F8", {"entities" : qUnion([Q0, Q1, Q2, Q3, Q4, Q5, Q6, Q7, Q8, Q9, Q10, Q11]), "radius" : 5 * mm, "tangentPropagation" : true, "allowEdgeOverflow" : false});
        }
        {
            var Q0;
            {var subQ0=sQuery(id+"F5.wireOp",EDGE,"E31");var subQ1=sQuery(id+"F5.wireOp",EDGE,"E13");var subQ2=makeQuery(id+"F5.imprint","INTERSECT",VERTEX,{"disambiguationData":[OD(0.0)],"derivedFrom":[subQ1,subQ0]});Q0=makeQuery(id+"F5.imprint","IMPRINT",FACE,{"disambiguationData":[TD([[makeQuery(id+"F5.imprint","IMPRINT",EDGE,{"disambiguationData":[TD([[subQ2,-1.0]])],"derivedFrom":subQ1}),-1.0]])]});}
            var Q1;
            {var subQ0=sQuery(id+"F5.wireOp",EDGE,"E31");var subQ1=sQuery(id+"F5.wireOp",EDGE,"E13");var subQ2=makeQuery(id+"F5.imprint","INTERSECT",VERTEX,{"disambiguationData":[OD(0.0)],"derivedFrom":[subQ1,subQ0]});Q1=makeQuery(id+"F5.imprint","IMPRINT",FACE,{"disambiguationData":[TD([[makeQuery(id+"F5.imprint","IMPRINT",EDGE,{"disambiguationData":[TD([[subQ2,-1.0]])],"derivedFrom":subQ1}),1.0]])]});}
            var Q2;
            {var subQ0=sQuery(id+"F5.wireOp",EDGE,"E32");var subQ1=sQuery(id+"F5.wireOp",EDGE,"E13");var subQ2=makeQuery(id+"F5.imprint","INTERSECT",VERTEX,{"disambiguationData":[OD(0.0)],"derivedFrom":[subQ1,subQ0]});Q2=makeQuery(id+"F5.imprint","IMPRINT",FACE,{"disambiguationData":[TD([[makeQuery(id+"F5.imprint","IMPRINT",EDGE,{"disambiguationData":[TD([[subQ2,-1.0]])],"derivedFrom":subQ1}),-1.0]])]});}
            var Q3;
            {var subQ0=sQuery(id+"F5.wireOp",EDGE,"E32");var subQ1=sQuery(id+"F5.wireOp",EDGE,"E13");var subQ2=makeQuery(id+"F5.imprint","INTERSECT",VERTEX,{"disambiguationData":[OD(0.0)],"derivedFrom":[subQ1,subQ0]});Q3=makeQuery(id+"F5.imprint","IMPRINT",FACE,{"disambiguationData":[TD([[makeQuery(id+"F5.imprint","IMPRINT",EDGE,{"disambiguationData":[TD([[subQ2,-1.0]])],"derivedFrom":subQ1}),1.0]])]});}
            var Q4;
            {var subQ0=sQuery(id+"F5.wireOp",EDGE,"E33");var subQ1=sQuery(id+"F5.wireOp",EDGE,"E13");var subQ2=makeQuery(id+"F5.imprint","INTERSECT",VERTEX,{"disambiguationData":[OD(0.0)],"derivedFrom":[subQ1,subQ0]});Q4=makeQuery(id+"F5.imprint","IMPRINT",FACE,{"disambiguationData":[TD([[makeQuery(id+"F5.imprint","IMPRINT",EDGE,{"disambiguationData":[TD([[subQ2,-1.0]])],"derivedFrom":subQ1}),1.0]])]});}
            var Q5;
            {var subQ0=sQuery(id+"F5.wireOp",EDGE,"E33");var subQ1=sQuery(id+"F5.wireOp",EDGE,"E13");var subQ2=makeQuery(id+"F5.imprint","INTERSECT",VERTEX,{"disambiguationData":[OD(0.0)],"derivedFrom":[subQ1,subQ0]});Q5=makeQuery(id+"F5.imprint","IMPRINT",FACE,{"disambiguationData":[TD([[makeQuery(id+"F5.imprint","IMPRINT",EDGE,{"disambiguationData":[TD([[subQ2,-1.0]])],"derivedFrom":subQ1}),-1.0]])]});}
            var Q6;
            {var subQ0=sQuery(id+"F5.wireOp",EDGE,"E34");var subQ1=sQuery(id+"F5.wireOp",EDGE,"E13");var subQ2=makeQuery(id+"F5.imprint","INTERSECT",VERTEX,{"disambiguationData":[OD(0.0)],"derivedFrom":[subQ1,subQ0]});Q6=makeQuery(id+"F5.imprint","IMPRINT",FACE,{"disambiguationData":[TD([[makeQuery(id+"F5.imprint","IMPRINT",EDGE,{"disambiguationData":[TD([[subQ2,-1.0]])],"derivedFrom":subQ1}),1.0]])]});}
            var Q7;
            {var subQ0=sQuery(id+"F5.wireOp",EDGE,"E34");var subQ1=sQuery(id+"F5.wireOp",EDGE,"E13");var subQ2=makeQuery(id+"F5.imprint","INTERSECT",VERTEX,{"disambiguationData":[OD(0.0)],"derivedFrom":[subQ1,subQ0]});Q7=makeQuery(id+"F5.imprint","IMPRINT",FACE,{"disambiguationData":[TD([[makeQuery(id+"F5.imprint","IMPRINT",EDGE,{"disambiguationData":[TD([[subQ2,-1.0]])],"derivedFrom":subQ1}),-1.0]])]});}
            var Q8;
            {var subQ1=sQuery(id+"F5.wireOp",EDGE,"E36.bottom");Q8=makeQuery(id+"F5.imprint","IMPRINT",FACE,{"disambiguationData":[TD([[makeQuery(id+"F5.imprint","IMPRINT",EDGE,{"derivedFrom":subQ1}),-1.0]])]});}
            var Q9;
            {var subQ0=sQuery(id+"F5.wireOp",EDGE,"E36.top");var subQ1=sQuery(id+"F5.wireOp",EDGE,"E13");var subQ2=makeQuery(id+"F5.imprint","INTERSECT",VERTEX,{"derivedFrom":[subQ1,subQ0]});Q9=makeQuery(id+"F5.imprint","IMPRINT",FACE,{"disambiguationData":[TD([[makeQuery(id+"F5.imprint","IMPRINT",EDGE,{"disambiguationData":[TD([[subQ2,-1.0]])],"derivedFrom":subQ1}),1.0]])]});}
            var Q10;
            {var subQ0=sQuery(id+"F5.wireOp",EDGE,"E35");var subQ1=sQuery(id+"F5.wireOp",EDGE,"E13");var subQ2=makeQuery(id+"F5.imprint","INTERSECT",VERTEX,{"disambiguationData":[OD(0.0)],"derivedFrom":[subQ1,subQ0]});Q10=makeQuery(id+"F5.imprint","IMPRINT",FACE,{"disambiguationData":[TD([[makeQuery(id+"F5.imprint","IMPRINT",EDGE,{"disambiguationData":[TD([[subQ2,-1.0]])],"derivedFrom":subQ1}),-1.0]])]});}
            var Q11;
            {var subQ0=sQuery(id+"F5.wireOp",EDGE,"E35");var subQ1=sQuery(id+"F5.wireOp",EDGE,"E13");var subQ2=makeQuery(id+"F5.imprint","INTERSECT",VERTEX,{"disambiguationData":[OD(0.0)],"derivedFrom":[subQ1,subQ0]});Q11=makeQuery(id+"F5.imprint","IMPRINT",FACE,{"disambiguationData":[TD([[makeQuery(id+"F5.imprint","IMPRINT",EDGE,{"disambiguationData":[TD([[subQ2,-1.0]])],"derivedFrom":subQ1}),1.0]])]});}
            extrude(context, id + "F9", {"entities" : qUnion([Q0, Q1, Q2, Q3, Q4, Q5, Q6, Q7, Q8, Q9, Q10, Q11]), "operationType" : NewBodyOperationType.ADD, "depth" : 8 * mm, "offsetDistance" : 25 * mm});
        }
        {
            var Q0;
            Q0=makeQuery(id+"F9.opExtrude","CAP_EDGE",EDGE,{"disambiguationData":[OSD([sQuery(id+"F5.wireOp",EDGE,"E35")])],"isStart":false});
            var Q1;
            Q1=makeQuery(id+"F9.opExtrude","CAP_FACE",FACE,{"disambiguationData":[OSD([sQuery(id+"F5.wireOp",EDGE,"E31")])],"isStart":false});
            var Q2;
            Q2=makeQuery(id+"F9.opExtrude","CAP_FACE",FACE,{"disambiguationData":[OSD([sQuery(id+"F5.wireOp",EDGE,"E32")])],"isStart":false});
            var Q3;
            Q3=makeQuery(id+"F9.opExtrude","CAP_FACE",FACE,{"disambiguationData":[OSD([sQuery(id+"F5.wireOp",EDGE,"E33")])],"isStart":false});
            var Q4;
            Q4=makeQuery(id+"F9.opExtrude","CAP_FACE",FACE,{"disambiguationData":[OSD([sQuery(id+"F5.wireOp",EDGE,"E34")])],"isStart":false});
            var Q5;
            Q5=makeQuery(id+"F9.opExtrude","CAP_EDGE",EDGE,{"disambiguationData":[OSD([sQuery(id+"F5.wireOp",EDGE,"E36.left")])],"isStart":false});
            var Q6;
            Q6=makeQuery(id+"F9.opExtrude","CAP_EDGE",EDGE,{"disambiguationData":[OSD([sQuery(id+"F5.wireOp",EDGE,"E36.right")])],"isStart":false});
            var Q7;
            Q7=makeQuery(id+"F9.opExtrude","CAP_EDGE",EDGE,{"disambiguationData":[OSD([sQuery(id+"F5.wireOp",EDGE,"E36.bottom")])],"isStart":false});
            var Q8;
            Q8=makeQuery(id+"F9.opExtrude","CAP_EDGE",EDGE,{"disambiguationData":[OSD([sQuery(id+"F5.wireOp",EDGE,"E36.top")])],"isStart":false});
            fillet(context, id + "F10", {"entities" : qUnion([Q0, Q1, Q2, Q3, Q4, Q5, Q6, Q7, Q8]), "radius" : .45 * mm, "tangentPropagation" : true, "allowEdgeOverflow" : false});
        }
        {
            var Q0;
            {var subQ0=sQuery(id+"F5.wireOp",EDGE,"E35");var subQ1=sQuery(id+"F5.wireOp",EDGE,"E13");var subQ2=makeQuery(id+"F5.imprint","INTERSECT",VERTEX,{"disambiguationData":[OD(0.0)],"derivedFrom":[subQ1,subQ0]});Q0=makeQuery(id+"F5.imprint","IMPRINT",FACE,{"disambiguationData":[TD([[makeQuery(id+"F5.imprint","IMPRINT",EDGE,{"disambiguationData":[TD([[subQ2,-1.0]])],"derivedFrom":subQ1}),-1.0]])]});}
            var Q1;
            {var subQ0=sQuery(id+"F5.wireOp",EDGE,"E35");var subQ1=sQuery(id+"F5.wireOp",EDGE,"E13");var subQ2=makeQuery(id+"F5.imprint","INTERSECT",VERTEX,{"disambiguationData":[OD(0.0)],"derivedFrom":[subQ1,subQ0]});Q1=makeQuery(id+"F5.imprint","IMPRINT",FACE,{"disambiguationData":[TD([[makeQuery(id+"F5.imprint","IMPRINT",EDGE,{"disambiguationData":[TD([[subQ2,-1.0]])],"derivedFrom":subQ1}),1.0]])]});}
            var Q2;
            {var subQ1=sQuery(id+"F5.wireOp",EDGE,"E36.bottom");Q2=makeQuery(id+"F5.imprint","IMPRINT",FACE,{"disambiguationData":[TD([[makeQuery(id+"F5.imprint","IMPRINT",EDGE,{"derivedFrom":subQ1}),-1.0]])]});}
            var Q3;
            {var subQ0=sQuery(id+"F5.wireOp",EDGE,"E36.top");var subQ1=sQuery(id+"F5.wireOp",EDGE,"E13");var subQ2=makeQuery(id+"F5.imprint","INTERSECT",VERTEX,{"derivedFrom":[subQ1,subQ0]});Q3=makeQuery(id+"F5.imprint","IMPRINT",FACE,{"disambiguationData":[TD([[makeQuery(id+"F5.imprint","IMPRINT",EDGE,{"disambiguationData":[TD([[subQ2,-1.0]])],"derivedFrom":subQ1}),1.0]])]});}
            var Q4;
            {var subQ0=sQuery(id+"F5.wireOp",EDGE,"E34");var subQ1=sQuery(id+"F5.wireOp",EDGE,"E13");var subQ2=makeQuery(id+"F5.imprint","INTERSECT",VERTEX,{"disambiguationData":[OD(0.0)],"derivedFrom":[subQ1,subQ0]});Q4=makeQuery(id+"F5.imprint","IMPRINT",FACE,{"disambiguationData":[TD([[makeQuery(id+"F5.imprint","IMPRINT",EDGE,{"disambiguationData":[TD([[subQ2,-1.0]])],"derivedFrom":subQ1}),1.0]])]});}
            var Q5;
            {var subQ0=sQuery(id+"F5.wireOp",EDGE,"E34");var subQ1=sQuery(id+"F5.wireOp",EDGE,"E13");var subQ2=makeQuery(id+"F5.imprint","INTERSECT",VERTEX,{"disambiguationData":[OD(0.0)],"derivedFrom":[subQ1,subQ0]});Q5=makeQuery(id+"F5.imprint","IMPRINT",FACE,{"disambiguationData":[TD([[makeQuery(id+"F5.imprint","IMPRINT",EDGE,{"disambiguationData":[TD([[subQ2,-1.0]])],"derivedFrom":subQ1}),-1.0]])]});}
            var Q6;
            {var subQ0=sQuery(id+"F5.wireOp",EDGE,"E33");var subQ1=sQuery(id+"F5.wireOp",EDGE,"E13");var subQ2=makeQuery(id+"F5.imprint","INTERSECT",VERTEX,{"disambiguationData":[OD(0.0)],"derivedFrom":[subQ1,subQ0]});Q6=makeQuery(id+"F5.imprint","IMPRINT",FACE,{"disambiguationData":[TD([[makeQuery(id+"F5.imprint","IMPRINT",EDGE,{"disambiguationData":[TD([[subQ2,-1.0]])],"derivedFrom":subQ1}),1.0]])]});}
            var Q7;
            {var subQ0=sQuery(id+"F5.wireOp",EDGE,"E33");var subQ1=sQuery(id+"F5.wireOp",EDGE,"E13");var subQ2=makeQuery(id+"F5.imprint","INTERSECT",VERTEX,{"disambiguationData":[OD(0.0)],"derivedFrom":[subQ1,subQ0]});Q7=makeQuery(id+"F5.imprint","IMPRINT",FACE,{"disambiguationData":[TD([[makeQuery(id+"F5.imprint","IMPRINT",EDGE,{"disambiguationData":[TD([[subQ2,-1.0]])],"derivedFrom":subQ1}),-1.0]])]});}
            var Q8;
            {var subQ0=sQuery(id+"F5.wireOp",EDGE,"E32");var subQ1=sQuery(id+"F5.wireOp",EDGE,"E13");var subQ2=makeQuery(id+"F5.imprint","INTERSECT",VERTEX,{"disambiguationData":[OD(0.0)],"derivedFrom":[subQ1,subQ0]});Q8=makeQuery(id+"F5.imprint","IMPRINT",FACE,{"disambiguationData":[TD([[makeQuery(id+"F5.imprint","IMPRINT",EDGE,{"disambiguationData":[TD([[subQ2,-1.0]])],"derivedFrom":subQ1}),1.0]])]});}
            var Q9;
            {var subQ0=sQuery(id+"F5.wireOp",EDGE,"E32");var subQ1=sQuery(id+"F5.wireOp",EDGE,"E13");var subQ2=makeQuery(id+"F5.imprint","INTERSECT",VERTEX,{"disambiguationData":[OD(0.0)],"derivedFrom":[subQ1,subQ0]});Q9=makeQuery(id+"F5.imprint","IMPRINT",FACE,{"disambiguationData":[TD([[makeQuery(id+"F5.imprint","IMPRINT",EDGE,{"disambiguationData":[TD([[subQ2,-1.0]])],"derivedFrom":subQ1}),-1.0]])]});}
            var Q10;
            {var subQ0=sQuery(id+"F5.wireOp",EDGE,"E31");var subQ1=sQuery(id+"F5.wireOp",EDGE,"E13");var subQ2=makeQuery(id+"F5.imprint","INTERSECT",VERTEX,{"disambiguationData":[OD(0.0)],"derivedFrom":[subQ1,subQ0]});Q10=makeQuery(id+"F5.imprint","IMPRINT",FACE,{"disambiguationData":[TD([[makeQuery(id+"F5.imprint","IMPRINT",EDGE,{"disambiguationData":[TD([[subQ2,-1.0]])],"derivedFrom":subQ1}),-1.0]])]});}
            var Q11;
            {var subQ0=sQuery(id+"F5.wireOp",EDGE,"E31");var subQ1=sQuery(id+"F5.wireOp",EDGE,"E13");var subQ2=makeQuery(id+"F5.imprint","INTERSECT",VERTEX,{"disambiguationData":[OD(0.0)],"derivedFrom":[subQ1,subQ0]});Q11=makeQuery(id+"F5.imprint","IMPRINT",FACE,{"disambiguationData":[TD([[makeQuery(id+"F5.imprint","IMPRINT",EDGE,{"disambiguationData":[TD([[subQ2,-1.0]])],"derivedFrom":subQ1}),1.0]])]});}
            extrude(context, id + "F11", {"entities" : qUnion([Q0, Q1, Q2, Q3, Q4, Q5, Q6, Q7, Q8, Q9, Q10, Q11]), "operationType" : NewBodyOperationType.REMOVE, "depth" : 1.8 * mm, "offsetDistance" : 25 * mm});
        }
        {
            var Q0;
            Q0=qCreatedBy(makeId("Top.planeOp"),FACE);
            var sketch = newSketch(context, id + "F12", { "sketchPlane" : qUnion([Q0])});
            skCircle(sketch, "E37", {"center": v(0, 0) * mm, "radius": 13.47 * mm});
            skSolve(sketch);
        }
        {
            var Q0;
            Q0=makeQuery(id+"F12.imprint","IMPRINT",FACE,{"disambiguationData":[TD([[makeQuery(id+"F12.imprint","IMPRINT",EDGE,{"derivedFrom":sQuery(id+"F12.wireOp",EDGE,"E37")}),1.0]])]});
            extrude(context, id + "F13", {"entities" : qUnion([Q0]), "operationType" : NewBodyOperationType.REMOVE, "depth" : 1 * mm, "offsetDistance" : 25 * mm});
        }
        {
            var Q0;
            {var subQ0=sQuery(id+"F0.wireOp",EDGE,"E9.right");var subQ1=sQuery(id+"F0.wireOp",EDGE,"E1.0");var subQ2=makeQuery(id+"F0.imprint","INTERSECT",VERTEX,{"disambiguationData":[OD(1.0)],"derivedFrom":[subQ1,subQ0]});Q0=makeQuery(id+"F0.imprint","IMPRINT",FACE,{"disambiguationData":[TD([[makeQuery(id+"F0.imprint","IMPRINT",EDGE,{"disambiguationData":[TD([[subQ2,-1.0]])],"derivedFrom":subQ1}),1.0]])]});}
            var Q1;
            {var subQ0=sQuery(id+"F0.wireOp",EDGE,"E2.left");var subQ1=sQuery(id+"F0.wireOp",EDGE,"E1.0");var subQ2=makeQuery(id+"F0.imprint","INTERSECT",VERTEX,{"disambiguationData":[OD(0.0)],"derivedFrom":[subQ1,subQ0]});Q1=makeQuery(id+"F0.imprint","IMPRINT",FACE,{"disambiguationData":[TD([[makeQuery(id+"F0.imprint","IMPRINT",EDGE,{"disambiguationData":[TD([[subQ2,-1.0]])],"derivedFrom":subQ1}),1.0]])]});}
            var Q2;
            {var subQ0=sQuery(id+"F0.wireOp",EDGE,"E2.right");var subQ1=sQuery(id+"F0.wireOp",EDGE,"E1.0");var subQ2=makeQuery(id+"F0.imprint","INTERSECT",VERTEX,{"disambiguationData":[OD(1.0)],"derivedFrom":[subQ1,subQ0]});Q2=makeQuery(id+"F0.imprint","IMPRINT",FACE,{"disambiguationData":[TD([[makeQuery(id+"F0.imprint","IMPRINT",EDGE,{"disambiguationData":[TD([[subQ2,-1.0]])],"derivedFrom":subQ1}),1.0]])]});}
            var Q3;
            {var subQ0=sQuery(id+"F0.wireOp",EDGE,"E8.left");var subQ1=sQuery(id+"F0.wireOp",EDGE,"E1.0");var subQ2=makeQuery(id+"F0.imprint","INTERSECT",VERTEX,{"disambiguationData":[OD(0.0)],"derivedFrom":[subQ1,subQ0]});Q3=makeQuery(id+"F0.imprint","IMPRINT",FACE,{"disambiguationData":[TD([[makeQuery(id+"F0.imprint","IMPRINT",EDGE,{"disambiguationData":[TD([[subQ2,-1.0]])],"derivedFrom":subQ1}),1.0]])]});}
            var Q4;
            {var subQ0=sQuery(id+"F0.wireOp",EDGE,"E9.left");var subQ1=sQuery(id+"F0.wireOp",EDGE,"E1.0");var subQ2=makeQuery(id+"F0.imprint","INTERSECT",VERTEX,{"disambiguationData":[OD(0.0)],"derivedFrom":[subQ1,subQ0]});Q4=makeQuery(id+"F0.imprint","IMPRINT",FACE,{"disambiguationData":[TD([[makeQuery(id+"F0.imprint","IMPRINT",EDGE,{"disambiguationData":[TD([[subQ2,-1.0]])],"derivedFrom":subQ1}),1.0]])]});}
            var Q5;
            {var subQ0=sQuery(id+"F0.wireOp",EDGE,"E7.top");var subQ1=sQuery(id+"F0.wireOp",EDGE,"E1.0");var subQ2=makeQuery(id+"F0.imprint","INTERSECT",VERTEX,{"disambiguationData":[OD(0.0)],"derivedFrom":[subQ1,subQ0]});Q5=makeQuery(id+"F0.imprint","IMPRINT",FACE,{"disambiguationData":[TD([[makeQuery(id+"F0.imprint","IMPRINT",EDGE,{"disambiguationData":[TD([[subQ2,-1.0]])],"derivedFrom":subQ1}),1.0]])]});}
            var Q6;
            {var subQ0=sQuery(id+"F0.wireOp",EDGE,"E6.top");var subQ1=sQuery(id+"F0.wireOp",EDGE,"E1.0");var subQ2=makeQuery(id+"F0.imprint","INTERSECT",VERTEX,{"disambiguationData":[OD(0.0)],"derivedFrom":[subQ1,subQ0]});Q6=makeQuery(id+"F0.imprint","IMPRINT",FACE,{"disambiguationData":[TD([[makeQuery(id+"F0.imprint","IMPRINT",EDGE,{"disambiguationData":[TD([[subQ2,-1.0]])],"derivedFrom":subQ1}),1.0]])]});}
            extrude(context, id + "F14", {"entities" : qUnion([Q0, Q1, Q2, Q3, Q4, Q5, Q6]), "operationType" : NewBodyOperationType.REMOVE, "depth" : 1 * mm, "offsetDistance" : 25 * mm});
        }
        {
            var Q0;
            Q0=makeQuery(id+"F14.boolean.opBoolean","COPY",EDGE,{"derivedFrom":makeQuery(id+"F14.opExtrude","SWEPT_EDGE",EDGE,{"disambiguationData":[OSD([sQuery(id+"F0.wireOp",EDGE,"E1.0"),sQuery(id+"F0.wireOp",EDGE,"E6.bottom")])]})});
            var Q1;
            Q1=makeQuery(id+"F14.boolean.opBoolean","COPY",EDGE,{"derivedFrom":makeQuery(id+"F14.opExtrude","SWEPT_EDGE",EDGE,{"disambiguationData":[OSD([sQuery(id+"F0.wireOp",EDGE,"E1.0"),sQuery(id+"F0.wireOp",EDGE,"E3.left")])]})});
            var Q2;
            Q2=makeQuery(id+"F14.boolean.opBoolean","COPY",EDGE,{"derivedFrom":makeQuery(id+"F14.opExtrude","SWEPT_EDGE",EDGE,{"disambiguationData":[OSD([sQuery(id+"F0.wireOp",EDGE,"E1.0"),sQuery(id+"F0.wireOp",EDGE,"E2.right")])]})});
            var Q3;
            Q3=makeQuery(id+"F14.boolean.opBoolean","COPY",EDGE,{"derivedFrom":makeQuery(id+"F14.opExtrude","SWEPT_EDGE",EDGE,{"disambiguationData":[OSD([sQuery(id+"F0.wireOp",EDGE,"E1.0"),sQuery(id+"F0.wireOp",EDGE,"E6.top")])]})});
            var Q4;
            Q4=makeQuery(id+"F14.boolean.opBoolean","COPY",EDGE,{"derivedFrom":makeQuery(id+"F14.opExtrude","SWEPT_EDGE",EDGE,{"disambiguationData":[OSD([sQuery(id+"F0.wireOp",EDGE,"E1.0"),sQuery(id+"F0.wireOp",EDGE,"E7.bottom")])]})});
            var Q5;
            {var subQ0=sQuery(id+"F0.wireOp",EDGE,"E9.right");var subQ1=sQuery(id+"F0.wireOp",EDGE,"E1.0");Q5=makeQuery(id+"F14.boolean.opBoolean","COPY",EDGE,{"derivedFrom":makeQuery(id+"F14.opExtrude","SWEPT_EDGE",EDGE,{"disambiguationData":[OSD([subQ1,subQ0]),TDD([makeQuery(id+"F0.imprint","INTERSECT",VERTEX,{"disambiguationData":[OD(0.0)],"derivedFrom":[subQ1,subQ0]})])]})});}
            var Q6;
            Q6=makeQuery(id+"F14.boolean.opBoolean","COPY",EDGE,{"derivedFrom":makeQuery(id+"F14.opExtrude","SWEPT_EDGE",EDGE,{"disambiguationData":[OSD([sQuery(id+"F0.wireOp",EDGE,"E1.0"),sQuery(id+"F0.wireOp",EDGE,"E9.left")])]})});
            var Q7;
            {var subQ0=sQuery(id+"F0.wireOp",EDGE,"E8.left");var subQ1=sQuery(id+"F0.wireOp",EDGE,"E1.0");Q7=makeQuery(id+"F14.boolean.opBoolean","COPY",EDGE,{"derivedFrom":makeQuery(id+"F14.opExtrude","SWEPT_EDGE",EDGE,{"disambiguationData":[OSD([subQ1,subQ0]),TDD([makeQuery(id+"F0.imprint","INTERSECT",VERTEX,{"disambiguationData":[OD(0.0)],"derivedFrom":[subQ1,subQ0]})])]})});}
            var Q8;
            Q8=makeQuery(id+"F14.boolean.opBoolean","COPY",EDGE,{"derivedFrom":makeQuery(id+"F14.opExtrude","SWEPT_EDGE",EDGE,{"disambiguationData":[OSD([sQuery(id+"F0.wireOp",EDGE,"E1.0"),sQuery(id+"F0.wireOp",EDGE,"E2.left")])]})});
            var Q9;
            {var subQ0=sQuery(id+"F0.wireOp",EDGE,"E7.top");var subQ1=sQuery(id+"F0.wireOp",EDGE,"E1.0");Q9=makeQuery(id+"F14.boolean.opBoolean","COPY",EDGE,{"derivedFrom":makeQuery(id+"F14.opExtrude","SWEPT_EDGE",EDGE,{"disambiguationData":[OSD([subQ1,subQ0]),TDD([makeQuery(id+"F0.imprint","INTERSECT",VERTEX,{"disambiguationData":[OD(1.0)],"derivedFrom":[subQ1,subQ0]})])]})});}
            var Q10;
            {var subQ0=sQuery(id+"F0.wireOp",EDGE,"E9.right");var subQ1=sQuery(id+"F0.wireOp",EDGE,"E1.0");Q10=makeQuery(id+"F14.boolean.opBoolean","COPY",EDGE,{"derivedFrom":makeQuery(id+"F14.opExtrude","SWEPT_EDGE",EDGE,{"disambiguationData":[OSD([subQ1,subQ0]),TDD([makeQuery(id+"F0.imprint","INTERSECT",VERTEX,{"disambiguationData":[OD(1.0)],"derivedFrom":[subQ1,subQ0]})])]})});}
            var Q11;
            {var subQ0=sQuery(id+"F0.wireOp",EDGE,"E8.left");var subQ1=sQuery(id+"F0.wireOp",EDGE,"E1.0");Q11=makeQuery(id+"F14.boolean.opBoolean","COPY",EDGE,{"derivedFrom":makeQuery(id+"F14.opExtrude","SWEPT_EDGE",EDGE,{"disambiguationData":[OSD([subQ1,subQ0]),TDD([makeQuery(id+"F0.imprint","INTERSECT",VERTEX,{"disambiguationData":[OD(1.0)],"derivedFrom":[subQ1,subQ0]})])]})});}
            var Q12;
            {var subQ0=sQuery(id+"F0.wireOp",EDGE,"E7.top");var subQ1=sQuery(id+"F0.wireOp",EDGE,"E1.0");Q12=makeQuery(id+"F14.boolean.opBoolean","COPY",EDGE,{"derivedFrom":makeQuery(id+"F14.opExtrude","SWEPT_EDGE",EDGE,{"disambiguationData":[OSD([subQ1,subQ0]),TDD([makeQuery(id+"F0.imprint","INTERSECT",VERTEX,{"disambiguationData":[OD(0.0)],"derivedFrom":[subQ1,subQ0]})])]})});}
            var Q13;
            Q13=makeQuery(id+"F14.boolean.opBoolean","COPY",EDGE,{"derivedFrom":makeQuery(id+"F14.opExtrude","SWEPT_EDGE",EDGE,{"disambiguationData":[OSD([sQuery(id+"F0.wireOp",EDGE,"E1.0"),sQuery(id+"F0.wireOp",EDGE,"E8.right")])]})});
            fillet(context, id + "F15", {"entities" : qUnion([Q0, Q1, Q2, Q3, Q4, Q5, Q6, Q7, Q8, Q9, Q10, Q11, Q12, Q13]), "radius" : 1 * mm, "tangentPropagation" : true, "allowEdgeOverflow" : false});
        }
    });
